# Revit family: DLB010002-V2
name_source: partatom
category: Appareils sanitaires
revit_build: Autodesk Revit 2015 (Build: 20140606_1530(x64)
units: mm (PartAtom-declared; Revit-internal decimal feet)

## types (1)
- DLB010002-V2
    Category = Basin mixer
    Commentaires du type = Deck-mounted time flow mixer
    Description = French manufacturer Delabie is a leader in the European sanitary ware market for non-domestic places. Water controls, solutions for disabled people, sanitary ware, for schools, leisure centres, offices, hospitals, airports…
    Elévation par défaut = 1219 mm
    Fabricant = DELABIE
    Features = Deck-mounted single control time flow basin mixer:
Soft-touch operation.
Temperature control and operation on the push-button.
Time flow ~7 sec.
Flow rate pre-set at 3 lpm at 3 bar, can be adjusted from 1.5 to 6 lpm.
Scale-resistant flow straightener.
Solid chrome-plated brass body.
PEX flexibles F3/8" with stopcocks, filters and non-return valves.
Fixing reinforced by 2 stainless steel rods. 
Adjustable maximum temperature limiter.
Ergonomic chrome-plated metal control.
10-year warranty.
    Finish = Chrome-plated
    FlowRate lpm = 3 lpm at 3 bar
    FlowRate lps = 0.05 lps at 3 bar
    Grade = ACS - BELGAQUA - PZH
    IntegralAccessory = Stopcocks, PEX flexibles
    IntegralAccessoryOptions = Thermostatic mixing valve
    ManufacturerName = DELABIE
    ManufacturerURL = http://www.delabie.com
    Material = Solid brass
    ModelNumber = 795000
    Modèle = TEMPOMIX
    Name = TEMPOMIX
    NominalHeight = 60 mm  [stored 0.19685 ft]
    NominalLength = 110 mm  [stored 0.360892 ft]
    Operation = Single control time flow mixer
    ProductInformation = http://www.delabie.com
    Radius = 15 mm  [stored 0.0492126 ft]
    SerialNumber = 3456330007962
    URL = http://www.delabie.com
    Version = V2
    WarrantyDescription = Any manufacturing defect
    WarrantyDurationUnit = 10 years
    WaterSupplyTemperatureMaximum = 55°C-85° (∆50°C : CW/HW)

note: [stored X ft] marks values corroborated as IEEE doubles in the binary element streams (Revit-internal decimal feet)

## geometry (parser evidence)
native form markers: Sweep x3
no freeform markers — native parametric forms only
